# Revit family: Тактильная полиуретановая плитка прямы полосы
name_source: partatom
category: Оборудование
revit_build: Autodesk Revit 2017 (Build: 20160225_1515(x64)
units: mm (PartAtom-declared; Revit-internal decimal feet)

## family parameters
Общий = Да
Основа = Грань
При загрузке вырезать с полостями = Да
Размер круглого соединителя = Использовать диаметр
Тип детали = Нормальный
Точка расчета площади = Нет

## types (2) — shared parameters
ADSK_Наименование = Тактильная плитка полиуретан с прямыми рельефными полосами (самоклеящаяся)
ADSK_Размер_Высота рифа = 5 мм
ADSK_Размер_Габариты = 300Х300
ADSK_Размер_Длина = 300 мм
ADSK_Размер_Толщина = 2 мм
ADSK_Размер_Ширина = 300 мм
ADSK_Тип рифов = Рельефные полосы
URL = http://tiflocentre.ru
Изготовитель = ТИФЛОЦЕНТР «ВЕРТИКАЛЬ»
Применение = Улица/Помещение
Стоимость = 742 $
zero-valued in all types: Отметка по умолчанию

## per-type parameters (varying)
| type | ADSK_Код изделия | ADSK_Материал наименование | ADSK_Материал плитки | Описание |
| Тактильная плитка полиуретан_Желтая | 10130-1-ZH | Полиуретан, цвет желтый | Вертикаль_Полиуретан_Желтый | Тактильная ПУ плитка с рельефными прямыми полосами используется для информирования о безопасном пути движения людей с ограничениями зрения. Желтый цвет является отличным контрастом к темной поверхности, что рекомендовано государственными стандартами. Тактильная ПУ плитка является устойчивой к перепадам температур и обладает высокими прочностными характеристиками, поэтому может монтироваться даже на улице. Особенность данного вида ПУ плитки - самоклеящаяся поверхность, что значительно упрощает монтаж. |
| Тактильная плитка полиуретановая_Черная | 10130-1-CH | Полиуретан, цвет черный | Вертикаль_Полиуретан_Черный | Тактильная плитка ПУ с рельефными параллельными полосами информирует людей с ограничениями зрения о движении без преград. Черный цвет служит отличным контрастом к светлой поверхности, что особенно важно для слабовидящих людей. В этом случае желтая плитка будет менее эффективна. Благодаря своим высоким прочностным и устойчивым характеристикам, тактильную ПУ плитку можно монтировать не только в помещениях, но и на улице. При этом ее легко монтировать к поверхности, так как она самоклеящаяся. Достаточно лишь хорошо очистить поверхность. Наша тактильная ПУ плитка рекомендована к применению гос. программой "Доступная среда" и одобрена ВОС. |
